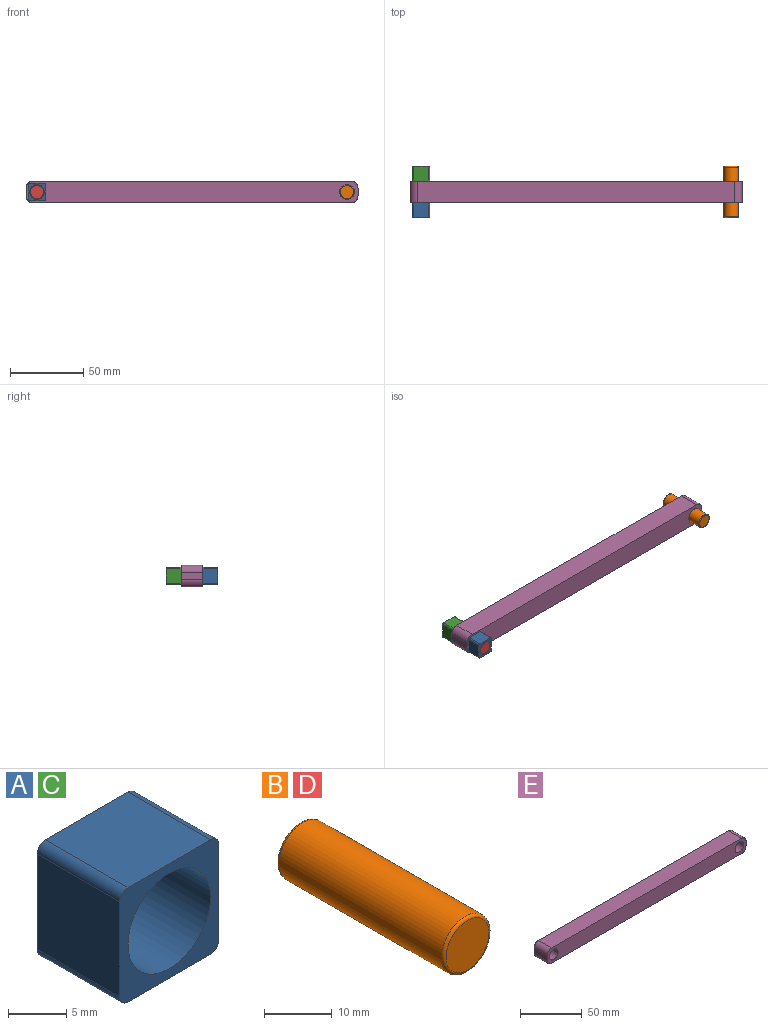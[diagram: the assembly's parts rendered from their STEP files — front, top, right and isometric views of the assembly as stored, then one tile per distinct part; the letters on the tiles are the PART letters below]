
ASSEMBLY  parts=5 mates=4
PART A: 11 faces, bbox 12x10x12 mm
  f0: plane 10x10mm, normal (1,0,0), area 100mm2, adj f5,f6,f7,f10
  f1: plane 10x10mm, normal (0,0,1), area 100mm2, adj f5,f6,f7,f8
  f2: plane 10x10mm, normal (-1,0,0), area 100mm2, adj f5,f6,f8,f9
  f3: cylinder r=5mm len=10mm, axis (0,1,0), area 314.2mm2, adj f5,f6
  f4: plane 10x10mm, normal (0,0,-1), area 100mm2, adj f5,f6,f9,f10
  f5: plane 12x12mm, normal (0,-1,0), area 64.6mm2, adj f0,f1,f2,f3,f4,f7,f8,f9
  f6: plane 12x12mm, normal (0,1,0), area 64.6mm2, adj f0,f1,f2,f3,f4,f7,f8,f9
  f7: cylinder r=1mm len=10mm, axis (0,1,0), area 15.7mm2, adj f0,f1,f5,f6
  f8: cylinder r=1mm len=10mm, axis (0,-1,0), area 15.7mm2, adj f1,f2,f5,f6
  f9: cylinder r=1mm len=10mm, axis (0,1,0), area 15.7mm2, adj f2,f4,f5,f6
  f10: cylinder r=1mm len=10mm, axis (0,-1,0), area 15.7mm2, adj f0,f4,f5,f6
PART B: 5 faces, bbox 10.8x35x10.8 mm
  f0: cylinder r=5mm len=34mm, axis (0,1,0), area 1068.1mm2, adj f3,f4
  f1: plane 9x9mm, normal (0,-1,0), area 63.6mm2, adj f4
  f2: plane 9x9mm, normal (0,1,0), area 63.6mm2, adj f3
  f3: torus R=4.5mm, axis (0,-1,0), area 23.8mm2, adj f0,f2
  f4: torus R=4.5mm, axis (0,-1,0), area 23.8mm2, adj f0,f1
PART C: same geometry as A
PART D: same geometry as B
PART E: 12 faces, bbox 227x15x15 mm
  f0: plane 15x5mm, normal (-1,0,0), area 75mm2, adj f6,f7,f8,f11
  f1: plane 217x15mm, normal (0,0,-1), area 3255mm2, adj f6,f7,f8,f9
  f2: plane 15x5mm, normal (1,0,0), area 75mm2, adj f6,f7,f9,f10
  f3: cylinder r=5mm len=15mm, axis (0,1,0), area 471.2mm2, adj f6,f7
  f4: plane 217x15mm, normal (0,0,1), area 3255mm2, adj f6,f7,f10,f11
  f5: cylinder r=5mm len=15mm, axis (0,1,0), area 471.2mm2, adj f6,f7
  f6: plane 227x15mm, normal (0,-1,0), area 3226.5mm2, adj f0,f1,f2,f3,f4,f5,f8,f9
  f7: plane 227x15mm, normal (0,1,0), area 3226.5mm2, adj f0,f1,f2,f3,f4,f5,f8,f9
  f8: cylinder r=5mm len=15mm, axis (0,-1,0), area 117.8mm2, adj f0,f1,f6,f7
  f9: cylinder r=5mm len=15mm, axis (0,1,0), area 117.8mm2, adj f1,f2,f6,f7
  f10: cylinder r=5mm len=15mm, axis (0,-1,0), area 117.8mm2, adj f2,f4,f6,f7
  f11: cylinder r=5mm len=15mm, axis (0,1,0), area 117.8mm2, adj f0,f4,f6,f7
PLACE A t=(-1.02,39.22,-20.83)mm
PLACE B t=(210.98,64.22,-20.83)mm
PLACE C t=(-1.02,64.22,-20.83)mm
PLACE D t=(-1.02,64.22,-20.83)mm
PLACE E t=(-1.02,54.22,-20.83)mm
MATE cylindrical C.f3 <-> D.f0  axis (0,1,0) through (-1.02,64.22,-20.83)mm
MATE fastened B.f0 <-> E.f3  axis (0,-1,0) through (210.98,29.22,-20.83)mm
MATE fastened D.f0 <-> E.f5  axis (0,-1,0) through (-1.02,29.22,-20.83)mm
MATE cylindrical A.f3 <-> D.f0  axis (0,-1,0) through (-1.02,29.22,-20.83)mm
